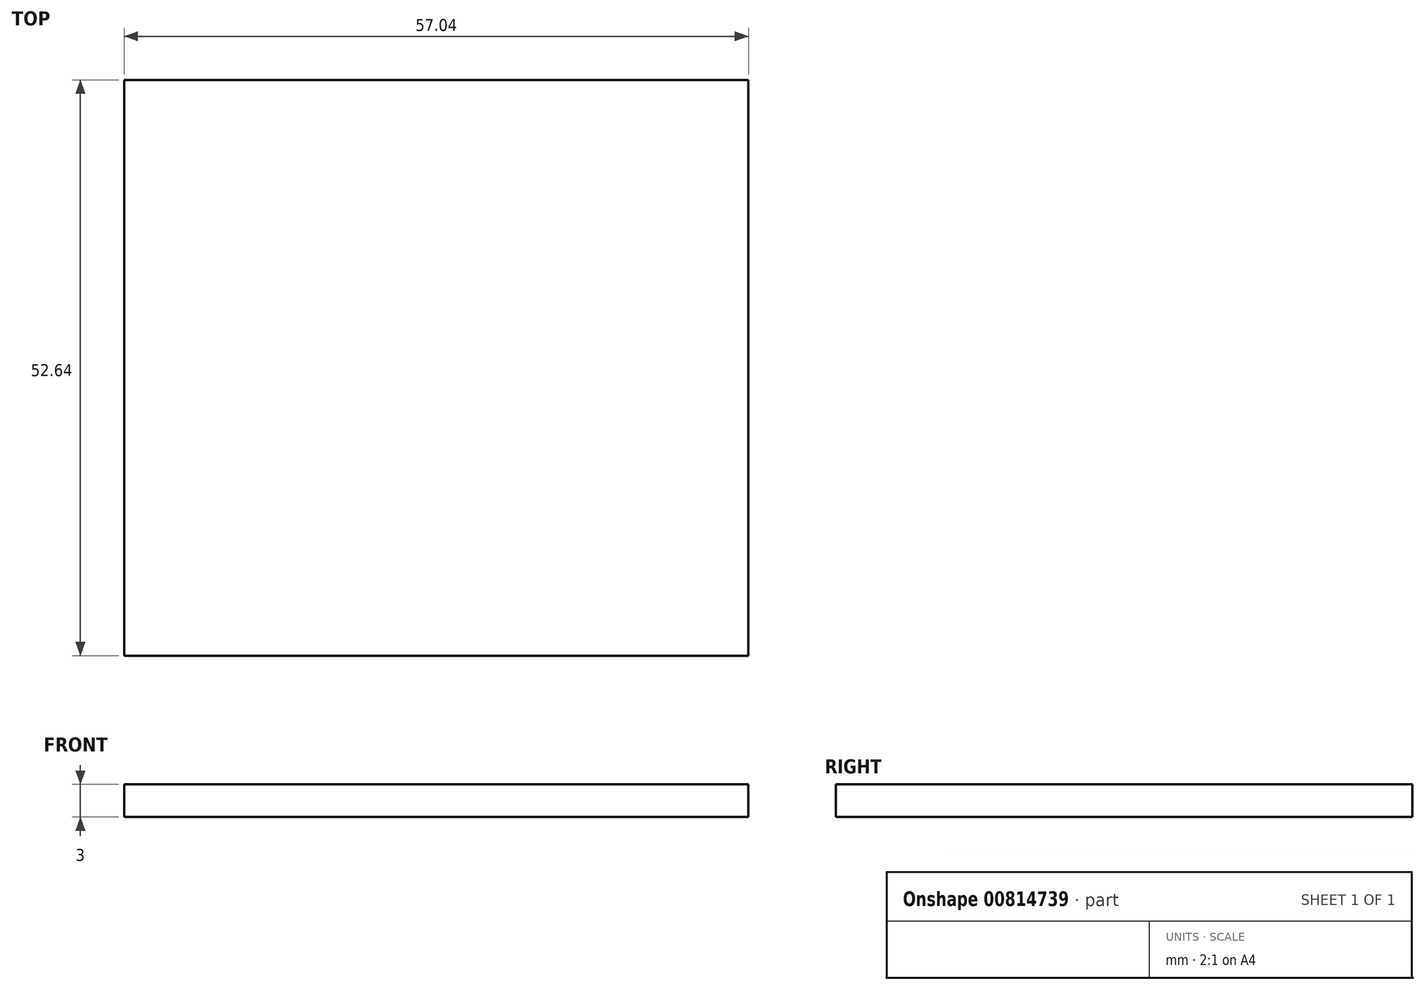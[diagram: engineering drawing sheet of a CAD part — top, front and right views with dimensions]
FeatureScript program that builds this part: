
annotation { "Feature Type Name" : "Feature", "Feature Type Description" : "" }
export const myFeature = defineFeature(function(context is Context, id is Id, definition is map)
    precondition{}
    {
        {
            var Q0;
            Q0=qCreatedBy(makeId("Top.planeOp"),FACE);
            var sketch = newSketch(context, id + "F0", { "sketchPlane" : qUnion([Q0])});
            skLineSegment(sketch, "E0.bottom", {"start": v(28.52, -26.32) * mm, "end": v(-28.52, -26.32) * mm});
            skLineSegment(sketch, "E0.top", {"start": v(28.52, 26.32) * mm, "end": v(-28.52, 26.32) * mm});
            skLineSegment(sketch, "E0.left", {"start": v(28.52, -26.32) * mm, "end": v(28.52, 26.32) * mm});
            skLineSegment(sketch, "E0.right", {"start": v(-28.52, -26.32) * mm, "end": v(-28.52, 26.32) * mm});
            skPoint(sketch, "E0.middle", {"position": v(0, 0) * mm});
            skSolve(sketch);
        }
        {
            var Q0;
            Q0=makeQuery(id+"F0.imprint","IMPRINT",FACE,{"disambiguationData":[TD([[makeQuery(id+"F0.imprint","IMPRINT",EDGE,{"derivedFrom":sQuery(id+"F0.wireOp",EDGE,"E0.bottom")}),-1.0]])]});
            extrude(context, id + "F1", {"entities" : qUnion([Q0]), "depth" : 3 * mm, "offsetDistance" : 25.4 * mm});
        }
    });
